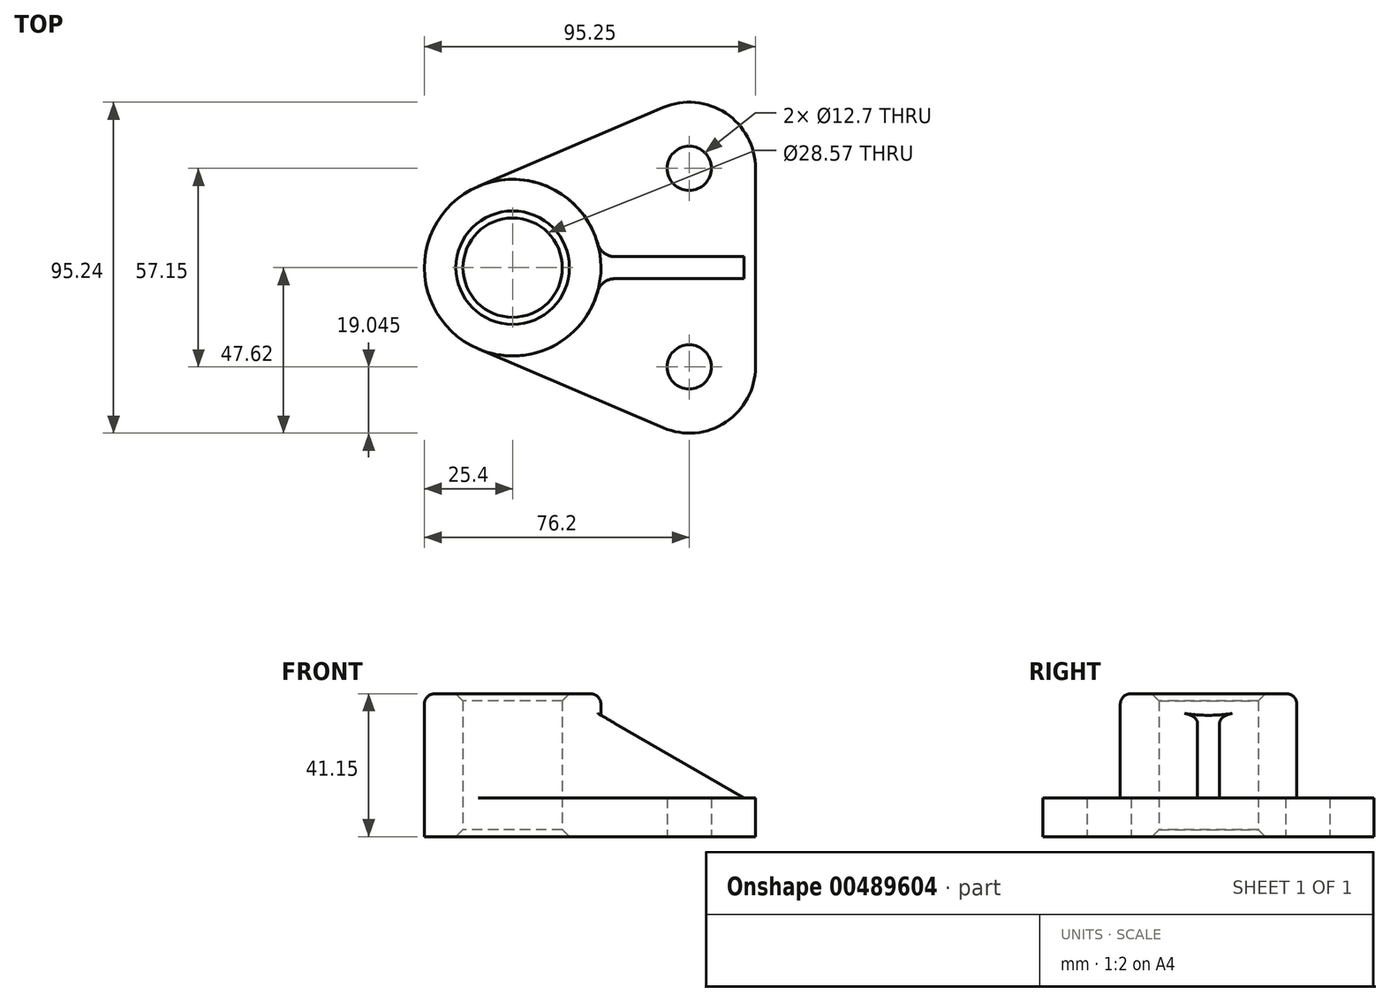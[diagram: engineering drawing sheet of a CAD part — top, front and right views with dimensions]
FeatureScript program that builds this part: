
annotation { "Feature Type Name" : "Feature", "Feature Type Description" : "" }
export const myFeature = defineFeature(function(context is Context, id is Id, definition is map)
    precondition{}
    {
        {
            var Q0;
            Q0=qCreatedBy(makeId("Top.planeOp"),FACE);
            var sketch = newSketch(context, id + "F0", { "sketchPlane" : qUnion([Q0])});
            skCircle(sketch, "E0", {"center": v(0, 0) * mm, "radius": 25.4 * mm});
            skLineSegment(sketch, "E1", {"start": v(0, 0) * mm, "end": v(123.62, 0) * mm, "construction": true});
            skPoint(sketch, "E2", {"position": v(50.8, -28.58) * mm});
            skPoint(sketch, "E3", {"position": v(50.8, 28.58) * mm});
            skCircle(sketch, "E4", {"center": v(50.8, -28.58) * mm, "radius": 6.35 * mm});
            skCircle(sketch, "E5", {"center": v(50.8, 28.58) * mm, "radius": 6.35 * mm});
            skArc(sketch, "E6", {"start": v(69.85, 28.58) * mm, "mid": v(61.3, 44.47) * mm, "end": v(43.33, 46.1) * mm});
            skArc(sketch, "E7", {"start": v(43.33, -46.1) * mm, "mid": v(61.3, -44.47) * mm, "end": v(69.85, -28.57) * mm});
            skCircle(sketch, "E8", {"center": v(0, 0) * mm, "radius": 14.29 * mm});
            skLineSegment(sketch, "E9", {"start": v(43.33, -46.1) * mm, "end": v(-9.97, -23.36) * mm});
            skLineSegment(sketch, "E10", {"start": v(43.33, 46.1) * mm, "end": v(-9.97, 23.36) * mm});
            skLineSegment(sketch, "E11", {"start": v(69.85, 28.58) * mm, "end": v(69.85, -28.57) * mm});
            skSolve(sketch);
        }
        {
            var Q0;
            Q0=makeQuery(id+"F0.imprint","IMPRINT",FACE,{"disambiguationData":[TD([[makeQuery(id+"F0.imprint","IMPRINT",EDGE,{"derivedFrom":sQuery(id+"F0.wireOp",EDGE,"E8")}),-1.0]])]});
            extrude(context, id + "F1", {"entities" : qUnion([Q0]), "depth" : 41.15 * mm});
        }
        {
            var Q0;
            Q0=makeQuery(id+"F0.imprint","IMPRINT",FACE,{"disambiguationData":[TD([[makeQuery(id+"F0.imprint","IMPRINT",EDGE,{"derivedFrom":sQuery(id+"F0.wireOp",EDGE,"E4")}),-1.0]])]});
            extrude(context, id + "F2", {"entities" : qUnion([Q0]), "operationType" : NewBodyOperationType.ADD, "depth" : 11.18 * mm});
        }
        {
            var Q0;
            Q0=qCreatedBy(makeId("Front.planeOp"),FACE);
            var sketch = newSketch(context, id + "F3", { "sketchPlane" : qUnion([Q0])});
            skLineSegment(sketch, "E12", {"start": v(66.55, 11.18) * mm, "end": v(22.64, 36.53) * mm});
            skLineSegment(sketch, "E13", {"start": v(66.55, 11.18) * mm, "end": v(22.64, 11.18) * mm});
            skLineSegment(sketch, "E14", {"start": v(22.64, 11.18) * mm, "end": v(22.64, 36.53) * mm});
            skSolve(sketch);
        }
        {
            var Q0;
            Q0=makeQuery(id+"F3.imprint","IMPRINT",FACE,{"disambiguationData":[TD([[makeQuery(id+"F3.imprint","IMPRINT",EDGE,{"derivedFrom":sQuery(id+"F3.wireOp",EDGE,"E12")}),1.0]])]});
            extrude(context, id + "F4", {"entities" : qUnion([Q0]), "operationType" : NewBodyOperationType.ADD, "endBound" : BoundingType.SYMMETRIC, "depth" : 6.35 * mm});
        }
        {
            var Q0;
            Q0=makeQuery(id+"F4.opExtrude","CAP_EDGE",EDGE,{"disambiguationData":[OSD([sQuery(id+"F3.wireOp",EDGE,"E13")])],"isStart":false});
            var Q1;
            {var subQ0=sQuery(id+"F0.wireOp",EDGE,"E0");var subQ1=sQuery(id+"F0.wireOp",EDGE,"E9");Q1=makeQuery(id+"F4.boolean.opBoolean","SPLIT",EDGE,{"disambiguationData":[TD([makeQuery(id+"F2.opExtrude","SWEPT_FACE",FACE,{"disambiguationData":[OSD([subQ1])]})])],"derivedFrom":makeQuery(id+"F2.opExtrude","CAP_EDGE",EDGE,{"disambiguationData":[OSD([subQ0])],"isStart":false})});}
            var Q2;
            Q2=makeQuery(id+"F4.boolean.opBoolean","INTERSECT",EDGE,{"derivedFrom":[makeQuery(id+"F1.opExtrude","SWEPT_FACE",FACE,{"disambiguationData":[OSD([sQuery(id+"F0.wireOp",EDGE,"E0")])]}),makeQuery(id+"F4.opExtrude","CAP_FACE",FACE,{"disambiguationData":[OSD([sQuery(id+"F3.wireOp",EDGE,"E12"),sQuery(id+"F3.wireOp",EDGE,"E13"),sQuery(id+"F3.wireOp",EDGE,"E14")])],"isStart":false})]});
            var Q3;
            Q3=makeQuery(id+"F4.boolean.opBoolean","INTERSECT",EDGE,{"derivedFrom":[makeQuery(id+"F1.opExtrude","SWEPT_FACE",FACE,{"disambiguationData":[OSD([sQuery(id+"F0.wireOp",EDGE,"E0")])]}),makeQuery(id+"F4.opExtrude","CAP_FACE",FACE,{"disambiguationData":[OSD([sQuery(id+"F3.wireOp",EDGE,"E12"),sQuery(id+"F3.wireOp",EDGE,"E13"),sQuery(id+"F3.wireOp",EDGE,"E14")])],"isStart":true})]});
            var Q4;
            {var subQ0=sQuery(id+"F0.wireOp",EDGE,"E0");var subQ1=sQuery(id+"F0.wireOp",EDGE,"E10");Q4=makeQuery(id+"F4.boolean.opBoolean","SPLIT",EDGE,{"disambiguationData":[TD([makeQuery(id+"F2.opExtrude","SWEPT_FACE",FACE,{"disambiguationData":[OSD([subQ1])]})])],"derivedFrom":makeQuery(id+"F2.opExtrude","CAP_EDGE",EDGE,{"disambiguationData":[OSD([subQ0])],"isStart":false})});}
            var Q5;
            Q5=makeQuery(id+"F4.opExtrude","CAP_EDGE",EDGE,{"disambiguationData":[OSD([sQuery(id+"F3.wireOp",EDGE,"E13")])],"isStart":true});
            fillet(context, id + "F5", {"entities" : qUnion([Q0, Q1, Q2, Q3, Q4, Q5]), "radius" : 5.08 * mm, "tangentPropagation" : true, "allowEdgeOverflow" : false});
        }
        {
            var Q0;
            Q0=makeQuery(id+"F1.opExtrude","CAP_EDGE",EDGE,{"disambiguationData":[OSD([sQuery(id+"F0.wireOp",EDGE,"E0")])],"isStart":false});
            fillet(context, id + "F6", {"entities" : qUnion([Q0]), "radius" : 3.05 * mm, "tangentPropagation" : true, "allowEdgeOverflow" : false});
        }
        {
            var Q0;
            Q0=makeQuery(id+"F1.opExtrude","CAP_EDGE",EDGE,{"disambiguationData":[OSD([sQuery(id+"F0.wireOp",EDGE,"E8")])],"isStart":false});
            chamfer(context, id + "F7", {"entities" : qUnion([Q0]), "chamferType" : ChamferType.OFFSET_ANGLE, "width" : 2.03 * mm, "oppositeDirection" : false, "angle" : 45 * degree, "tangentPropagation" : true});
        }
        {
            var Q0;
            Q0=makeQuery(id+"F1.opExtrude","CAP_EDGE",EDGE,{"disambiguationData":[OSD([sQuery(id+"F0.wireOp",EDGE,"E8")])],"isStart":true});
            chamfer(context, id + "F8", {"entities" : qUnion([Q0]), "chamferType" : ChamferType.OFFSET_ANGLE, "width" : 2.03 * mm, "oppositeDirection" : false, "angle" : 45 * degree, "tangentPropagation" : true});
        }
    });
